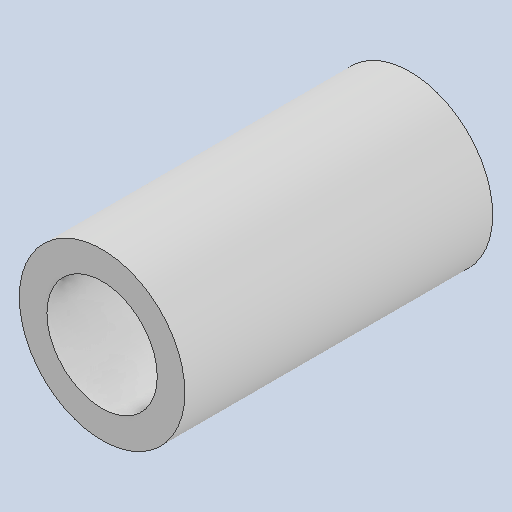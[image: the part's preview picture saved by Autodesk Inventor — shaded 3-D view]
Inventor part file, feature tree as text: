
AUTODESK INVENTOR PART (.ipt)
format: ipt  version: 2022 (Build 260153000, 153)  size: 102,400 bytes
history: native  units: mm
features: other x3, reference x2, extrude x1, sketch x1
ambient origin geometry x8: Origin, YZ Plane, XZ Plane, XY Plane, X Axis, Y Axis, Z Axis, Center Point
bodies: Solid1 (feature_tree)
feature tree (7):
  extrude  "Extrusion1"  Depth=16.738mm
  sketch  "Sketch1"  dims[d0=6.0mm d1=9.0mm d2=16.738mm d3=0.0mm]
  reference  "Reference1"
  reference  "Reference2"
  other  "<userpath>\Documents\Inventor\etchasketch\Knobass.iam"
  other  "Knobass.iam"
  other  "Part4:1"
